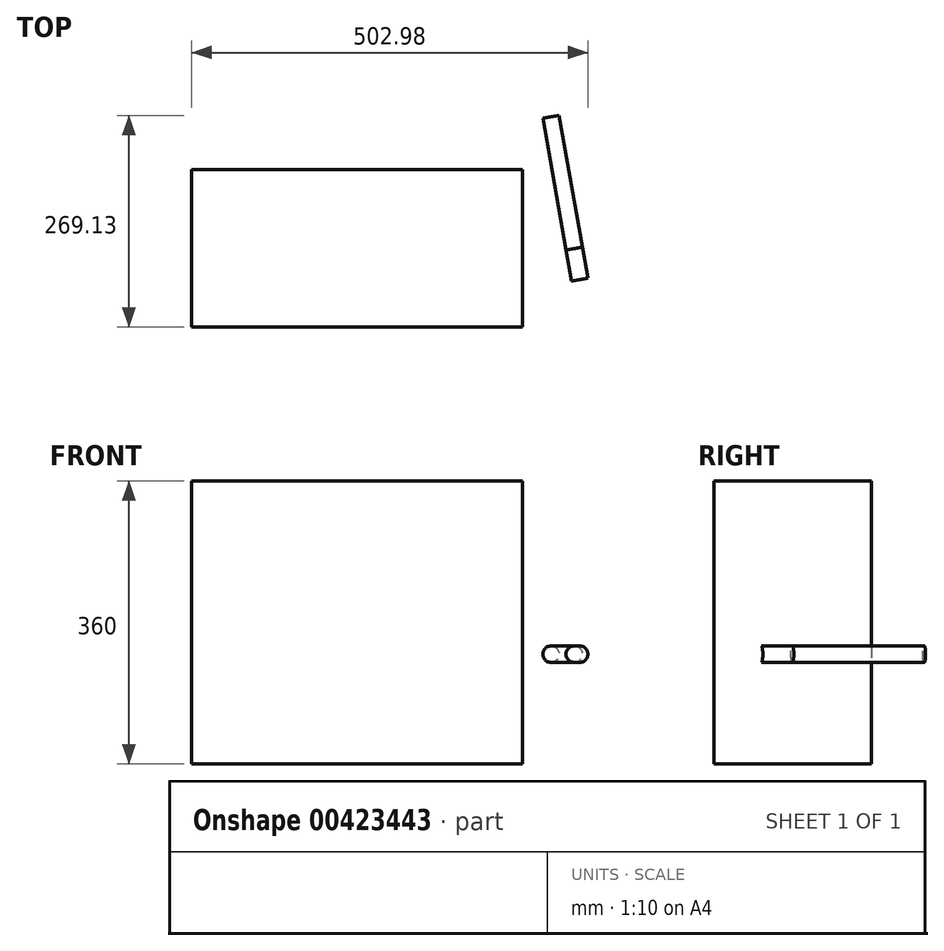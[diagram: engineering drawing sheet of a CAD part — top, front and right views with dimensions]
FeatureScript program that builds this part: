
annotation { "Feature Type Name" : "Feature", "Feature Type Description" : "" }
export const myFeature = defineFeature(function(context is Context, id is Id, definition is map)
    precondition{}
    {
        {
            var Q0;
            Q0=qCreatedBy(makeId("Front.planeOp"),FACE);
            var sketch = newSketch(context, id + "F0", { "sketchPlane" : qUnion([Q0])});
            skLineSegment(sketch, "E0.bottom", {"start": v(-114.65, 226.49) * mm, "end": v(305.35, 226.49) * mm});
            skLineSegment(sketch, "E0.top", {"start": v(-114.65, -133.51) * mm, "end": v(305.35, -133.51) * mm});
            skLineSegment(sketch, "E0.left", {"start": v(-114.65, 226.49) * mm, "end": v(-114.65, -133.51) * mm});
            skLineSegment(sketch, "E0.right", {"start": v(305.35, 226.49) * mm, "end": v(305.35, -133.51) * mm});
            skSolve(sketch);
        }
        {
            var Q0;
            Q0=makeQuery(id+"F0.imprint","IMPRINT",FACE,{"disambiguationData":[TD([[makeQuery(id+"F0.imprint","IMPRINT",EDGE,{"derivedFrom":sQuery(id+"F0.wireOp",EDGE,"E0.bottom")}),-1.0]])]});
            extrude(context, id + "F1", {"entities" : qUnion([Q0]), "depth" : 200 * mm});
        }
        {
            var Q0;
            Q0=makeQuery(id+"F1.opExtrude","CAP_FACE",FACE,{"disambiguationData":[OSD([sQuery(id+"F0.wireOp",EDGE,"E0.bottom"),sQuery(id+"F0.wireOp",EDGE,"E0.top"),sQuery(id+"F0.wireOp",EDGE,"E0.left"),sQuery(id+"F0.wireOp",EDGE,"E0.right")])],"isStart":true});
            var sketch = newSketch(context, id + "F2", { "sketchPlane" : qUnion([Q0])});
            skCircle(sketch, "E1", {"center": v(-352.66, 6.15) * mm, "radius": 10.5 * mm});
            skSolve(sketch);
        }
        {
            var Q0;
            Q0=makeQuery(id+"F2.imprint","IMPRINT",FACE,{"disambiguationData":[TD([[makeQuery(id+"F2.imprint","IMPRINT",EDGE,{"derivedFrom":sQuery(id+"F2.wireOp",EDGE,"E1")}),1.0]])]});
            var Q1;
            Q1=sQuery(id+"F2.wireOp",EDGE,"E1");
            extrude(context, id + "F3", {"entities" : qUnion([Q0]), "surfaceEntities" : qUnion([Q1]), "depth" : 170 * mm});
        }
        {
            var Q0;
            Q0=makeQuery(id+"F3.opExtrude","SWEPT_BODY",BODY,{"disambiguationData":[OSD([sQuery(id+"F2.wireOp",EDGE,"E1")])]});
            transform(context, id + "F4", {"entities" : qUnion([Q0]), "transformType" : TransformType.TRANSLATION_3D, "dx" : 0 * mm, "dy" : -110 * mm, "dz" : 0 * mm, "makeCopy" : false});
        }
        {
            var Q0;
            Q0=makeQuery(id+"F3.opExtrude","SWEPT_BODY",BODY,{"disambiguationData":[OSD([sQuery(id+"F2.wireOp",EDGE,"E1")])]});
            var Q1;
            Q1=makeQuery(id+"F1.opExtrude","CAP_EDGE",EDGE,{"disambiguationData":[OSD([sQuery(id+"F0.wireOp",EDGE,"E0.right")])],"isStart":true});
            transform(context, id + "F5", {"entities" : qUnion([Q0]), "transformType" : TransformType.ROTATION, "transformAxis" : qUnion([Q1]), "angle" : 350 * degree, "makeCopy" : false});
        }
        {
            var Q0;
            Q0=makeQuery(id+"F3.opExtrude","CAP_FACE",FACE,{"disambiguationData":[OSD([sQuery(id+"F2.wireOp",EDGE,"E1")])],"isStart":true});
            extrude(context, id + "F6", {"entities" : qUnion([Q0]), "depth" : 40 * mm});
        }
    });
